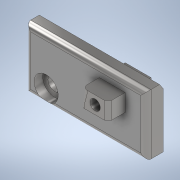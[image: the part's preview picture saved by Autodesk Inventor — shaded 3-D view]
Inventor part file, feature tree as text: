
AUTODESK INVENTOR PART (.ipt)
format: ipt  version: 2021 (Build 250183000, 183)  size: 195,072 bytes
history: native  units: mm
features: extrude x5, sketch x5, fillet x2, chamfer x2, other x1
ambient origin geometry x8: Origin, YZ Plane, XZ Plane, XY Plane, X Axis, Y Axis, Z Axis, Center Point
bodies: Body1 (feature_tree)
feature tree (15):
  other  "Sólido1"
  extrude  "Extrusão1"  Depth=35.0mm
  extrude  "Extrusão2"  Depth=8.0mm
  extrude  "Extrusão3"  Depth=10.0mm TaperAngle=0.0deg
  extrude  "Extrusão4"  Depth=10.0mm
  extrude  "Extrusão5"  Depth=6.0mm
  fillet  "Arredondamento1"  Radius=10.0mm
  fillet  "Arredondamento2"  Radius=6.0mm
  chamfer  "Chanfro1"  Distance=15.0mm
  chamfer  "Chanfro2"  Distance=14.0mm
  sketch  "Esboço1"  dims[d0=70.0mm d1=35.0mm]
  sketch  "Esboço2"  dims[d2=8.0mm d3=8.0mm]
  sketch  "Esboço3"  dims[d4=12.0mm d5=10.0mm d6=0.0mm]
  sketch  "Esboço4"  dims[d7=15.0mm d8=10.0mm]
  sketch  "Esboço5"  dims[d9=6.0mm d10=12.0mm d11=10.0mm d12=0.0mm d13=6.0mm d14=15.0mm d15=0.0mm d16=14.0mm d17=5.0mm d18=0.0mm d19=5.0mm d20=0.0mm d21=3.0mm d22=3.0mm d23=1.0mm d24=2.0mm d25=2.0mm d26=45.0deg d27=2.0mm d28=3.0mm d29=45.0deg]
